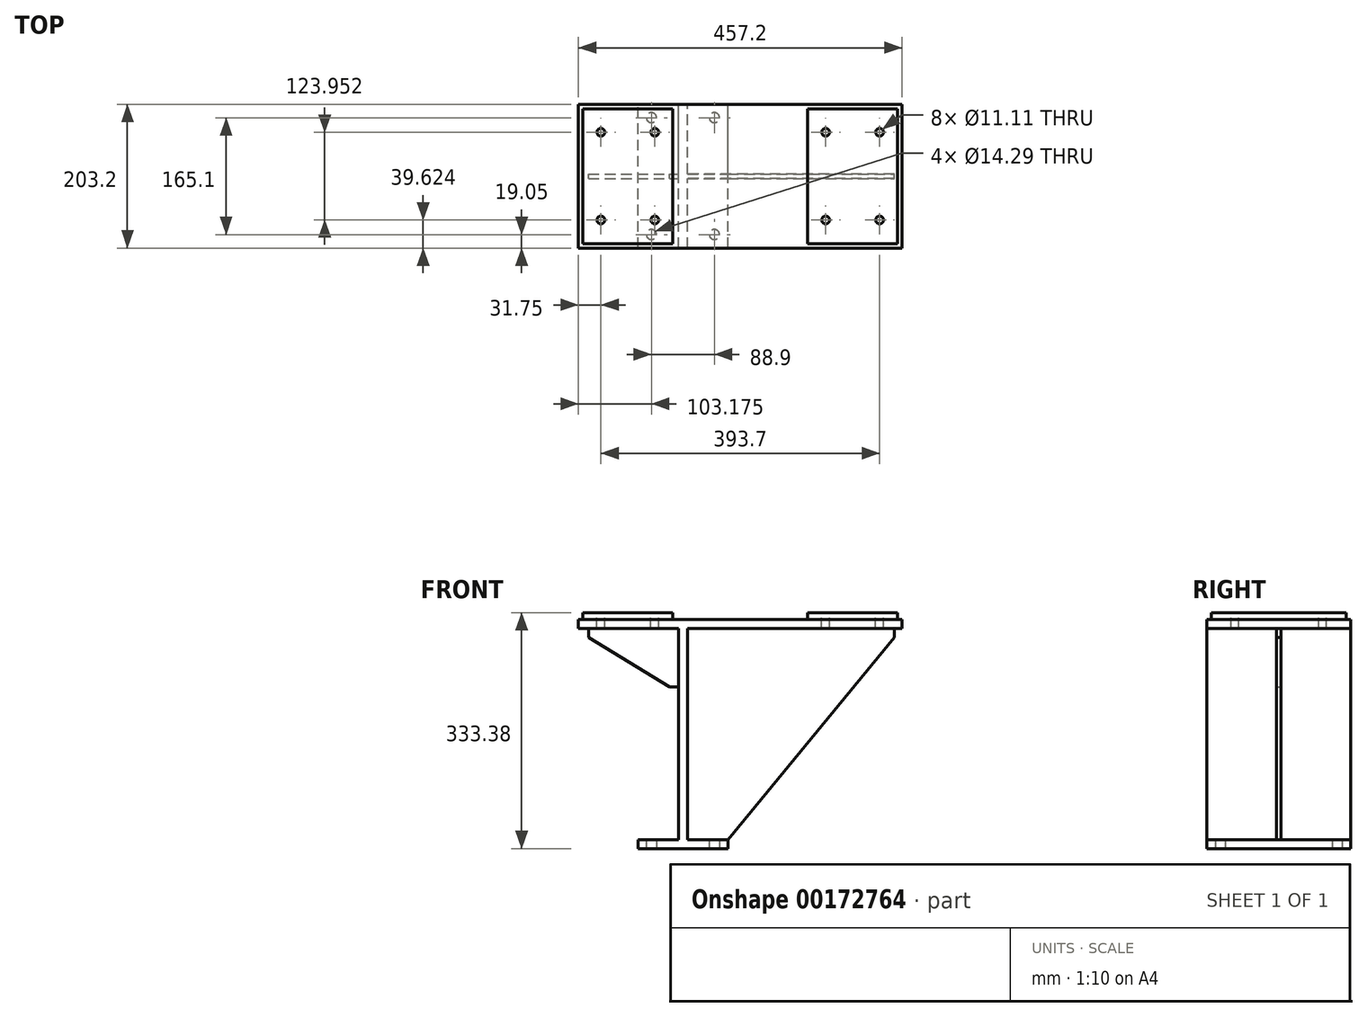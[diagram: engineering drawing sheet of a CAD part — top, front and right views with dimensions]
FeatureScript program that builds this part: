
annotation { "Feature Type Name" : "Feature", "Feature Type Description" : "" }
export const myFeature = defineFeature(function(context is Context, id is Id, definition is map)
    precondition{}
    {
        {
            var Q0;
            Q0=qCreatedBy(makeId("Top.planeOp"),FACE);
            var sketch = newSketch(context, id + "F0", { "sketchPlane" : qUnion([Q0])});
            skLineSegment(sketch, "E0.rect.bottom", {"start": v(-228.6, 101.6) * mm, "end": v(228.6, 101.6) * mm});
            skLineSegment(sketch, "E0.rect.top", {"start": v(-228.6, -101.6) * mm, "end": v(228.6, -101.6) * mm});
            skLineSegment(sketch, "E0.rect.left", {"start": v(-228.6, 101.6) * mm, "end": v(-228.6, -101.6) * mm});
            skLineSegment(sketch, "E0.rect.right", {"start": v(228.6, 101.6) * mm, "end": v(228.6, -101.6) * mm});
            skPoint(sketch, "E0.rect.middle", {"position": v(0, 0) * mm});
            skSolve(sketch);
        }
        {
            var Q0;
            Q0=qSketchRegion(id+"F0",true);
            extrude(context, id + "F1", {"entities" : qUnion([Q0]), "oppositeDirection" : true, "depth" : 12.7 * mm});
        }
        {
            var Q0;
            Q0=makeQuery(id+"F1.opExtrude","CAP_FACE",FACE,{"disambiguationData":[OSD([sQuery(id+"F0.wireOp",EDGE,"E0.rect.bottom"),sQuery(id+"F0.wireOp",EDGE,"E0.rect.top"),sQuery(id+"F0.wireOp",EDGE,"E0.rect.left"),sQuery(id+"F0.wireOp",EDGE,"E0.rect.right")])],"isStart":true});
            var sketch = newSketch(context, id + "F2", { "sketchPlane" : qUnion([Q0])});
            skLineSegment(sketch, "E1.0", {"start": v(222.25, 95.25) * mm, "end": v(95.25, 95.25) * mm});
            skLineSegment(sketch, "E1.1", {"start": v(222.25, -95.25) * mm, "end": v(222.25, 95.25) * mm});
            skLineSegment(sketch, "E1.2", {"start": v(-222.25, -95.25) * mm, "end": v(-95.25, -95.25) * mm});
            skLineSegment(sketch, "E1.3", {"start": v(-222.25, 95.25) * mm, "end": v(-222.25, -95.25) * mm});
            skLineSegment(sketch, "E2.0", {"start": v(95.25, -95.25) * mm, "end": v(95.25, 95.25) * mm});
            skLineSegment(sketch, "E3.0", {"start": v(-95.25, 95.25) * mm, "end": v(-95.25, -95.25) * mm});
            skLineSegment(sketch, "E4.trimOffspring", {"start": v(-95.25, 95.25) * mm, "end": v(-222.25, 95.25) * mm});
            skLineSegment(sketch, "E5.trimOffspring", {"start": v(95.25, -95.25) * mm, "end": v(222.25, -95.25) * mm});
            skSolve(sketch);
        }
        {
            var Q0;
            Q0=qSketchRegion(id+"F2",true);
            extrude(context, id + "F3", {"entities" : qUnion([Q0]), "operationType" : NewBodyOperationType.ADD, "depth" : 9.52 * mm});
        }
        {
            var Q0;
            Q0=makeQuery(id+"F3.opExtrude","CAP_FACE",FACE,{"disambiguationData":[OSD([sQuery(id+"F2.wireOp",EDGE,"E1.2"),sQuery(id+"F2.wireOp",EDGE,"E1.3"),sQuery(id+"F2.wireOp",EDGE,"E3.0"),sQuery(id+"F2.wireOp",EDGE,"E4.trimOffspring")])],"isStart":false});
            var sketch = newSketch(context, id + "F4", { "sketchPlane" : qUnion([Q0])});
            skLineSegment(sketch, "E6", {"start": v(-222.25, 0) * mm, "end": v(243.7, 0) * mm, "construction": true});
            skPoint(sketch, "E6.endSnap0", {"position": v(-95.25, 0) * mm});
            skLineSegment(sketch, "E7", {"start": v(-158.75, -95.25) * mm, "end": v(-158.75, 95.25) * mm, "construction": true});
            skLineSegment(sketch, "E8.0.0", {"start": v(222.25, -95.25) * mm, "end": v(222.25, 95.25) * mm, "construction": true});
            skLineSegment(sketch, "E8.0.1", {"start": v(222.25, 95.25) * mm, "end": v(95.25, 95.25) * mm, "construction": true});
            skLineSegment(sketch, "E8.0.2", {"start": v(95.25, 95.25) * mm, "end": v(95.25, -95.25) * mm, "construction": true});
            skLineSegment(sketch, "E8.0.3", {"start": v(95.25, -95.25) * mm, "end": v(222.25, -95.25) * mm, "construction": true});
            skLineSegment(sketch, "E9", {"start": v(158.75, -95.25) * mm, "end": v(158.75, 95.25) * mm, "construction": true});
            skLineSegment(sketch, "E10.0", {"start": v(-222.25, 61.98) * mm, "end": v(243.7, 61.98) * mm, "construction": true});
            skLineSegment(sketch, "E11.0", {"start": v(-222.25, -61.98) * mm, "end": v(243.7, -61.98) * mm, "construction": true});
            skLineSegment(sketch, "E12.0", {"start": v(-196.85, -95.25) * mm, "end": v(-196.85, 95.25) * mm, "construction": true});
            skLineSegment(sketch, "E13.0", {"start": v(-120.65, -95.25) * mm, "end": v(-120.65, 95.25) * mm, "construction": true});
            skLineSegment(sketch, "E14.0", {"start": v(120.65, -95.25) * mm, "end": v(120.65, 95.25) * mm, "construction": true});
            skLineSegment(sketch, "E15.0", {"start": v(196.85, -95.25) * mm, "end": v(196.85, 95.25) * mm, "construction": true});
            skPoint(sketch, "E16", {"position": v(-196.85, 61.98) * mm});
            skPoint(sketch, "E17", {"position": v(-120.65, 61.98) * mm});
            skPoint(sketch, "E18", {"position": v(-120.65, -61.98) * mm});
            skPoint(sketch, "E19", {"position": v(-196.85, -61.98) * mm});
            skPoint(sketch, "E20", {"position": v(120.65, 61.98) * mm});
            skPoint(sketch, "E21", {"position": v(196.85, 61.98) * mm});
            skPoint(sketch, "E22", {"position": v(196.85, -61.98) * mm});
            skPoint(sketch, "E23", {"position": v(120.65, -61.98) * mm});
            skSolve(sketch);
        }
        {
            var Q0;
            Q0=sQuery(id+"F4.wireOp",VERTEX,"E16");
            var Q1;
            Q1=sQuery(id+"F4.wireOp",VERTEX,"E17");
            var Q2;
            Q2=sQuery(id+"F4.wireOp",VERTEX,"E19");
            var Q3;
            Q3=sQuery(id+"F4.wireOp",VERTEX,"E18");
            var Q4;
            Q4=sQuery(id+"F4.wireOp",VERTEX,"E20");
            var Q5;
            Q5=sQuery(id+"F4.wireOp",VERTEX,"E21");
            var Q6;
            Q6=sQuery(id+"F4.wireOp",VERTEX,"E23");
            var Q7;
            Q7=sQuery(id+"F4.wireOp",VERTEX,"E22");
            var Q8;
            Q8=makeQuery(id+"F1.opExtrude","SWEPT_BODY",BODY,{"disambiguationData":[OSD([sQuery(id+"F0.wireOp",EDGE,"E0.rect.bottom"),sQuery(id+"F0.wireOp",EDGE,"E0.rect.top"),sQuery(id+"F0.wireOp",EDGE,"E0.rect.left"),sQuery(id+"F0.wireOp",EDGE,"E0.rect.right")])]});
            hole(context, id + "F5", {"style" : HoleStyle.SIMPLE, "holeDiameter" : 11.1 * mm, "endStyle" : HoleEndStyle.THROUGH, "locations" : qUnion([Q0, Q1, Q2, Q3, Q4, Q5, Q6, Q7]), "scope" : qUnion([Q8])});
        }
        {
            var Q0;
            Q0=qCreatedBy(makeId("Front.planeOp"),FACE);
            var sketch = newSketch(context, id + "F6", { "sketchPlane" : qUnion([Q0])});
            skLineSegment(sketch, "E24.0", {"start": v(-228.6, -12.7) * mm, "end": v(-228.6, 0) * mm, "construction": true});
            skLineSegment(sketch, "E25.0", {"start": v(-228.6, -12.7) * mm, "end": v(228.6, -12.7) * mm, "construction": true});
            skLineSegment(sketch, "E26", {"start": v(-228.6, -12.7) * mm, "end": v(-228.6, -311.15) * mm, "construction": true});
            skLineSegment(sketch, "E27.0", {"start": v(-80.98, -12.7) * mm, "end": v(-80.98, -311.15) * mm, "construction": true});
            skLineSegment(sketch, "E28.0", {"start": v(-87.33, -12.7) * mm, "end": v(-87.33, -311.15) * mm});
            skLineSegment(sketch, "E29.0", {"start": v(-74.63, -12.7) * mm, "end": v(-74.63, -311.15) * mm});
            skLineSegment(sketch, "E30.0", {"start": v(-214.33, -12.7) * mm, "end": v(-214.33, -25.4) * mm});
            skLineSegment(sketch, "E31.0", {"start": v(-228.6, -25.4) * mm, "end": v(-214.33, -25.4) * mm});
            skLineSegment(sketch, "E32.0", {"start": v(-228.6, -95.25) * mm, "end": v(-214.33, -95.25) * mm});
            skLineSegment(sketch, "E33", {"start": v(-214.33, -25.4) * mm, "end": v(-100.03, -95.25) * mm});
            skLineSegment(sketch, "E34.trimOffspring", {"start": v(-100.03, -95.25) * mm, "end": v(-87.33, -95.25) * mm});
            skLineSegment(sketch, "E35.trimOffspring", {"start": v(-214.33, -95.25) * mm, "end": v(-214.33, -311.15) * mm});
            skLineSegment(sketch, "E36", {"start": v(-214.33, -12.7) * mm, "end": v(-87.33, -12.7) * mm});
            skSolve(sketch);
        }
        {
            var Q0;
            Q0=qSketchRegion(id+"F6",true);
            extrude(context, id + "F7", {"entities" : qUnion([Q0]), "operationType" : NewBodyOperationType.ADD, "endBound" : BoundingType.SYMMETRIC, "depth" : 6.35 * mm});
        }
        {
            var Q0;
            Q0=qCreatedBy(makeId("Front.planeOp"),FACE);
            var sketch = newSketch(context, id + "F8", { "sketchPlane" : qUnion([Q0])});
            skLineSegment(sketch, "E37.0", {"start": v(217.47, -12.7) * mm, "end": v(217.47, -311.15) * mm});
            skLineSegment(sketch, "E38.0", {"start": v(-74.63, -12.7) * mm, "end": v(-74.63, -311.15) * mm});
            skLineSegment(sketch, "E39.0", {"start": v(-17.48, -12.7) * mm, "end": v(-17.48, -311.15) * mm});
            skLineSegment(sketch, "E40.0", {"start": v(-228.6, -25.4) * mm, "end": v(228.6, -25.4) * mm});
            skLineSegment(sketch, "E41", {"start": v(-74.63, -311.15) * mm, "end": v(-17.48, -311.15) * mm});
            skLineSegment(sketch, "E42", {"start": v(-17.48, -311.15) * mm, "end": v(217.47, -25.4) * mm});
            skLineSegment(sketch, "E43", {"start": v(217.47, -25.4) * mm, "end": v(217.47, -12.7) * mm});
            skLineSegment(sketch, "E44", {"start": v(217.47, -12.7) * mm, "end": v(-74.63, -12.7) * mm});
            skSolve(sketch);
        }
        {
            var Q0;
            Q0=qSketchRegion(id+"F8",true);
            extrude(context, id + "F9", {"entities" : qUnion([Q0]), "operationType" : NewBodyOperationType.ADD, "endBound" : BoundingType.SYMMETRIC, "depth" : 6.35 * mm});
        }
        {
            var Q0;
            Q0=qCreatedBy(makeId("Front.planeOp"),FACE);
            var sketch = newSketch(context, id + "F10", { "sketchPlane" : qUnion([Q0])});
            skLineSegment(sketch, "E45.0", {"start": v(-74.63, -12.7) * mm, "end": v(-74.63, -311.15) * mm});
            skLineSegment(sketch, "E46.0", {"start": v(-87.33, -12.7) * mm, "end": v(-87.33, -311.15) * mm});
            skLineSegment(sketch, "E47.0", {"start": v(-228.6, -12.7) * mm, "end": v(228.6, -12.7) * mm});
            skLineSegment(sketch, "E48", {"start": v(-87.33, -311.15) * mm, "end": v(-74.63, -311.15) * mm});
            skSolve(sketch);
        }
        {
            var Q0;
            Q0=qSketchRegion(id+"F10",true);
            extrude(context, id + "F11", {"entities" : qUnion([Q0]), "operationType" : NewBodyOperationType.ADD, "endBound" : BoundingType.SYMMETRIC, "depth" : 203.2 * mm});
        }
        {
            var Q0;
            Q0=qCreatedBy(makeId("Front.planeOp"),FACE);
            var sketch = newSketch(context, id + "F12", { "sketchPlane" : qUnion([Q0])});
            skLineSegment(sketch, "E49.0", {"start": v(-74.63, -311.15) * mm, "end": v(-17.48, -311.15) * mm});
            skLineSegment(sketch, "E50.bottom", {"start": v(-17.48, -311.15) * mm, "end": v(-144.48, -311.15) * mm});
            skLineSegment(sketch, "E50.top", {"start": v(-17.48, -323.85) * mm, "end": v(-144.48, -323.85) * mm});
            skLineSegment(sketch, "E50.left", {"start": v(-17.48, -311.15) * mm, "end": v(-17.48, -323.85) * mm});
            skLineSegment(sketch, "E50.right", {"start": v(-144.48, -311.15) * mm, "end": v(-144.48, -323.85) * mm});
            skSolve(sketch);
        }
        {
            var Q0;
            Q0=qSketchRegion(id+"F12",true);
            extrude(context, id + "F13", {"entities" : qUnion([Q0]), "operationType" : NewBodyOperationType.ADD, "endBound" : BoundingType.SYMMETRIC, "depth" : 203.2 * mm});
        }
        {
            var Q0;
            Q0=makeQuery(id+"F13.opExtrude","SWEPT_FACE",FACE,{"disambiguationData":[OSD([sQuery(id+"F12.wireOp",EDGE,"E50.top")])]});
            var sketch = newSketch(context, id + "F14", { "sketchPlane" : qUnion([Q0])});
            skLineSegment(sketch, "E51", {"start": v(-80.98, 101.6) * mm, "end": v(-80.98, -101.6) * mm, "construction": true});
            skLineSegment(sketch, "E52", {"start": v(-230.25, 0) * mm, "end": v(5.19, 0) * mm, "construction": true});
            skLineSegment(sketch, "E53.0", {"start": v(-125.43, 101.6) * mm, "end": v(-125.43, -101.6) * mm, "construction": true});
            skLineSegment(sketch, "E54.0", {"start": v(-230.25, 82.55) * mm, "end": v(5.19, 82.55) * mm, "construction": true});
            skPoint(sketch, "E55", {"position": v(-125.43, 82.55) * mm});
            skPoint(sketch, "E56.MirrorP", {"position": v(-36.53, 82.55) * mm});
            skPoint(sketch, "E57.MirrorP", {"position": v(-125.43, -82.55) * mm});
            skPoint(sketch, "E58.MirrorP", {"position": v(-36.53, -82.55) * mm});
            skSolve(sketch);
        }
        {
            var Q0;
            Q0=sQuery(id+"F14.wireOp",VERTEX,"E55");
            var Q1;
            Q1=sQuery(id+"F14.wireOp",VERTEX,"E57.MirrorP");
            var Q2;
            Q2=sQuery(id+"F14.wireOp",VERTEX,"E56.MirrorP");
            var Q3;
            Q3=sQuery(id+"F14.wireOp",VERTEX,"E58.MirrorP");
            var Q4;
            Q4=makeQuery(id+"F1.opExtrude","SWEPT_BODY",BODY,{"disambiguationData":[OSD([sQuery(id+"F0.wireOp",EDGE,"E0.rect.bottom"),sQuery(id+"F0.wireOp",EDGE,"E0.rect.top"),sQuery(id+"F0.wireOp",EDGE,"E0.rect.left"),sQuery(id+"F0.wireOp",EDGE,"E0.rect.right")])]});
            hole(context, id + "F15", {"style" : HoleStyle.SIMPLE, "holeDiameter" : 14.29 * mm, "endStyle" : HoleEndStyle.BLIND, "holeDepth" : 38.1 * mm, "locations" : qUnion([Q0, Q1, Q2, Q3]), "scope" : qUnion([Q4])});
        }
    });
